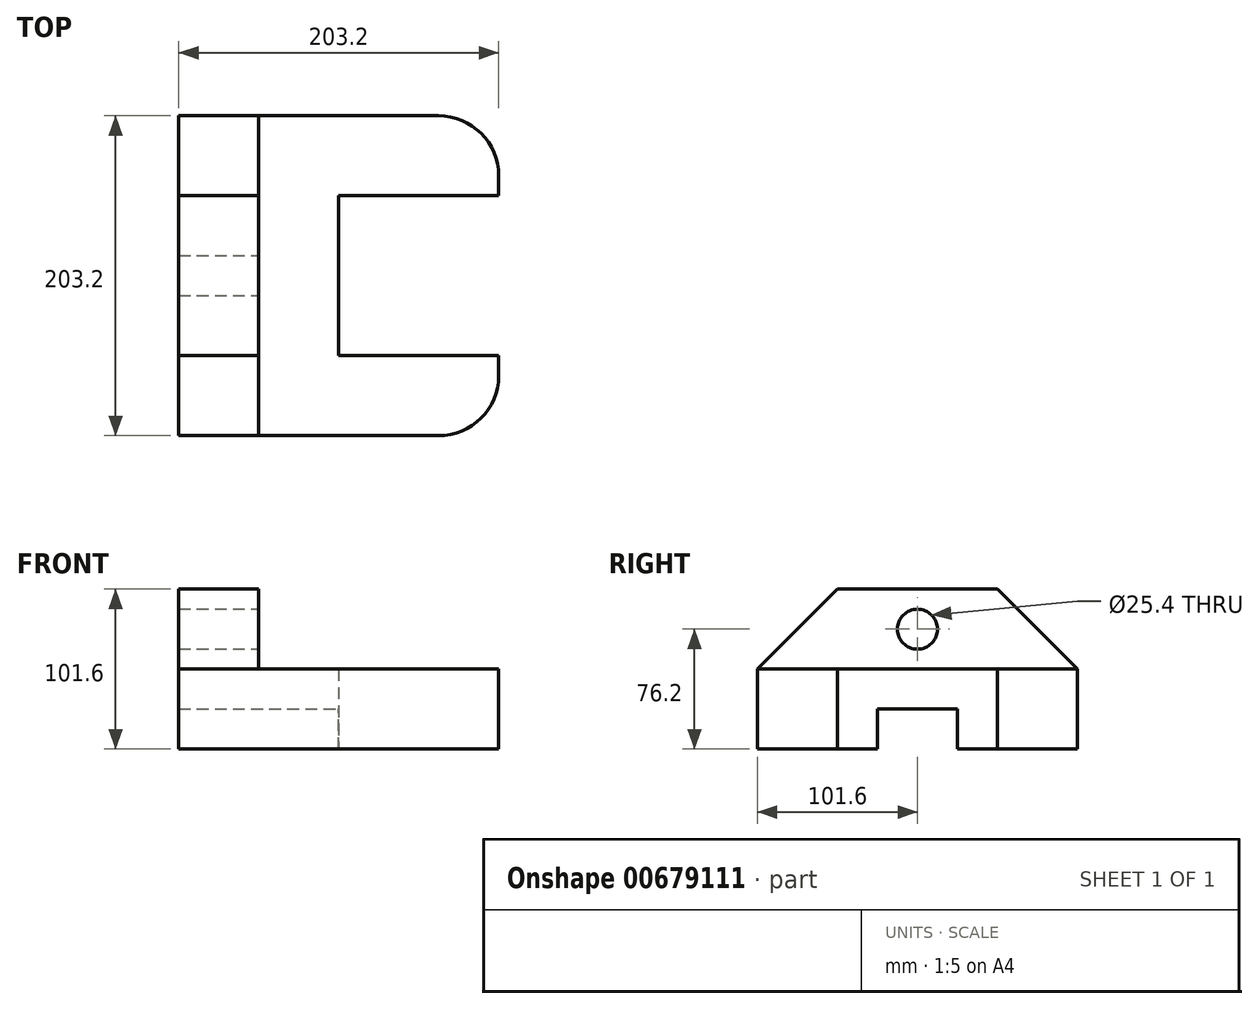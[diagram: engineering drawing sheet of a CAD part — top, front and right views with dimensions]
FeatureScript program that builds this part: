
annotation { "Feature Type Name" : "Feature", "Feature Type Description" : "" }
export const myFeature = defineFeature(function(context is Context, id is Id, definition is map)
    precondition{}
    {
        {
            var Q0;
            Q0=qCreatedBy(makeId("Top.planeOp"),FACE);
            var sketch = newSketch(context, id + "F0", { "sketchPlane" : qUnion([Q0])});
            skLineSegment(sketch, "E0", {"start": v(0, 203.2) * mm, "end": v(0, 0) * mm});
            skLineSegment(sketch, "E1", {"start": v(0, 0) * mm, "end": v(165.1, 0) * mm});
            skLineSegment(sketch, "E2", {"start": v(203.2, 38.1) * mm, "end": v(203.2, 50.8) * mm});
            skLineSegment(sketch, "E3", {"start": v(203.2, 50.8) * mm, "end": v(101.6, 50.8) * mm});
            skLineSegment(sketch, "E4", {"start": v(101.6, 50.8) * mm, "end": v(101.6, 152.4) * mm});
            skLineSegment(sketch, "E5", {"start": v(101.6, 152.4) * mm, "end": v(203.2, 152.4) * mm});
            skLineSegment(sketch, "E6", {"start": v(203.2, 152.4) * mm, "end": v(203.2, 165.1) * mm});
            skLineSegment(sketch, "E7", {"start": v(165.1, 203.2) * mm, "end": v(0, 203.2) * mm});
            skPoint(sketch, "E8.visualSharp", {"position": v(203.2, 203.2) * mm});
            skArc(sketch, "E8.filletArc", {"start": v(203.2, 165.1) * mm, "mid": v(192.04, 192.04) * mm, "end": v(165.1, 203.2) * mm});
            skPoint(sketch, "E9.visualSharp", {"position": v(203.2, 0) * mm});
            skArc(sketch, "E9.filletArc", {"start": v(165.1, 0) * mm, "mid": v(192.04, 11.16) * mm, "end": v(203.2, 38.1) * mm});
            skSolve(sketch);
        }
        {
            var Q0;
            Q0=makeQuery(id+"F0.imprint","IMPRINT",FACE,{"disambiguationData":[TD([[makeQuery(id+"F0.imprint","IMPRINT",EDGE,{"derivedFrom":sQuery(id+"F0.wireOp",EDGE,"E0")}),1.0]])]});
            extrude(context, id + "F1", {"entities" : qUnion([Q0]), "depth" : 50.8 * mm, "offsetDistance" : 25.4 * mm});
        }
        {
            var Q0;
            Q0=qCreatedBy(makeId("Right.planeOp"),FACE);
            var sketch = newSketch(context, id + "F2", { "sketchPlane" : qUnion([Q0])});
            skLineSegment(sketch, "E10", {"start": v(50.8, 101.6) * mm, "end": v(152.4, 101.6) * mm});
            skLineSegment(sketch, "E11", {"start": v(152.4, 101.6) * mm, "end": v(203.2, 50.8) * mm});
            skLineSegment(sketch, "E12", {"start": v(50.8, 101.6) * mm, "end": v(0, 50.8) * mm});
            skLineSegment(sketch, "E13", {"start": v(203.2, 50.8) * mm, "end": v(0, 50.8) * mm});
            skSolve(sketch);
        }
        {
            var Q0;
            Q0=makeQuery(id+"F2.imprint","IMPRINT",FACE,{"disambiguationData":[TD([[makeQuery(id+"F2.imprint","IMPRINT",EDGE,{"derivedFrom":sQuery(id+"F2.wireOp",EDGE,"E10")}),-1.0]])]});
            extrude(context, id + "F3", {"entities" : qUnion([Q0]), "operationType" : NewBodyOperationType.ADD, "depth" : 50.8 * mm, "offsetDistance" : 25.4 * mm});
        }
        {
            var Q0;
            Q0=makeQuery(id+"F3.opExtrude","CAP_FACE",FACE,{"disambiguationData":[OSD([sQuery(id+"F2.wireOp",EDGE,"E10"),sQuery(id+"F2.wireOp",EDGE,"E11"),sQuery(id+"F2.wireOp",EDGE,"E12"),sQuery(id+"F2.wireOp",EDGE,"E13")])],"isStart":false});
            var sketch = newSketch(context, id + "F4", { "sketchPlane" : qUnion([Q0])});
            skCircle(sketch, "E14", {"center": v(101.6, 76.2) * mm, "radius": 12.7 * mm});
            skSolve(sketch);
        }
        {
            var Q0;
            Q0=makeQuery(id+"F4.imprint","IMPRINT",FACE,{"disambiguationData":[TD([[makeQuery(id+"F4.imprint","IMPRINT",EDGE,{"derivedFrom":sQuery(id+"F4.wireOp",EDGE,"E14")}),1.0]])]});
            extrude(context, id + "F5", {"entities" : qUnion([Q0]), "operationType" : NewBodyOperationType.REMOVE, "oppositeDirection" : true, "depth" : 50.8 * mm, "offsetDistance" : 25.4 * mm});
        }
        {
            var Q0;
            Q0=makeQuery(id+"F1.opExtrude","SWEPT_FACE",FACE,{"disambiguationData":[OSD([sQuery(id+"F0.wireOp",EDGE,"E4")])]});
            var sketch = newSketch(context, id + "F6", { "sketchPlane" : qUnion([Q0])});
            skLineSegment(sketch, "E15", {"start": v(76.2, 0) * mm, "end": v(76.2, 25.4) * mm});
            skLineSegment(sketch, "E16", {"start": v(76.2, 25.4) * mm, "end": v(127, 25.4) * mm});
            skLineSegment(sketch, "E17", {"start": v(127, 25.4) * mm, "end": v(127, 0) * mm});
            skSolve(sketch);
        }
        {
            var Q0;
            {var subQ0=sQuery(id+"F6.wireOp",EDGE,"E15");Q0=makeQuery(id+"F6.imprint","IMPRINT",FACE,{"disambiguationData":[TD([[makeQuery(id+"F6.imprint","IMPRINT",EDGE,{"derivedFrom":subQ0}),-1.0]])]});}
            extrude(context, id + "F7", {"entities" : qUnion([Q0]), "operationType" : NewBodyOperationType.REMOVE, "oppositeDirection" : true, "depth" : 101.6 * mm, "offsetDistance" : 25.4 * mm});
        }
    });
